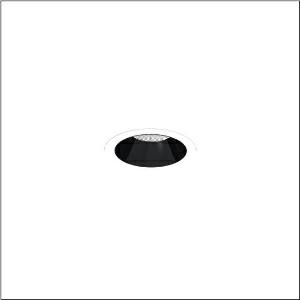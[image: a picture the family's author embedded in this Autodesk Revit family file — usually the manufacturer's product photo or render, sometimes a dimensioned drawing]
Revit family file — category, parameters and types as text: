
# Revit family: lunis_21_m_51db17ec91c
name_source: partatom
category: Lighting Fixtures
units: mm (PartAtom-declared; Revit-internal decimal feet)

## family parameters
Cut with Voids When Loaded = No
Host = Face
Light Source = No
Part Type = Normal
Room Calculation Point = No
Round Connector Dimension = Use Diameter
Shared = No

## types (1)
- --- (1 x LED, 3340 lm, 25.5 W, 4000K)
    Apparent Load = 26 VA
    CIE Flux Codes = 95 100 100 100 100
    Color Rendering = 80
    Color Temperature = 4000K
    Default Elevation = 1800 mm
    Description = Lunis 21,  M, downlight, light control with lens, of PMMA, anti glare with reflector, of PC, light emission: direct distribution, LED rated luminous flux: 1.540lm, light colour: 830/840/865, with terminal, 5-pole, mains connection: 220..240V, AC/DC, 0/50..60Hz, housing, round, of diecast aluminium, traffic white (RAL 9016), diameter: 115mm, clamping range: 1..40mm, protection rating (complete): IP20, protection rating (on room side): IP54, insulation class (complete): insulation class II (safety insulation), certification: CE, impact resistance: IK03, packaging unit: 1 piece
    Height = 0 mm  [stored 0 ft]
    Lamp = 1 x LED
    Lamp Light Flux = 3340 lm
    Lamp Power = 25.5 W
    Lamp count = 1
    Length = 115 mm
    Luminous efficacy = 131 lm/W
    Manufacturer = Siteco
    ModVariant = No
    Model = 51DB17EC91C
    Mounting Place = Ceiling
    Mounting Type = Recessed
    Number of Poles = 1
    OnlyDefault = Yes
    Power Factor = 1
    Product Name = Lunis 21 M
    Product group = downlight
    ProductGroupID = 400
    Protection Class = Protection class II
    Protection Degree = IP 20
    RLX_Detail_Level = 1
    RLX_Emergency_Light_Flux = 0 lm
    RLX_Emergency_Type = 0
    RLX_Emergency_Type_DB = No
    RlxData = <blob elided: 11465 chars, md5=9bf741b8>
    Socket = socket
    Standby Power = 0 W
    System Light Flux = 3340 lm
    System Power = 26 W
    Type Comments = individual setting: colour temperature 4000K, luminous flux: 100 % | (ON | ON | OFF | OFF) | 700 mA
    Type Image = l_1290854.jpg
    URL = http://relux.com
    VarID = @adj_017697
    Voltage = 0 V
    Weight = 0.00 kg
    Width = 0 mm  [stored 0 ft]

note: [stored X ft] marks values corroborated as IEEE doubles in the binary element streams (Revit-internal decimal feet)

## geometry (parser evidence)
native form markers: Sweep x9
no freeform markers — native parametric forms only
